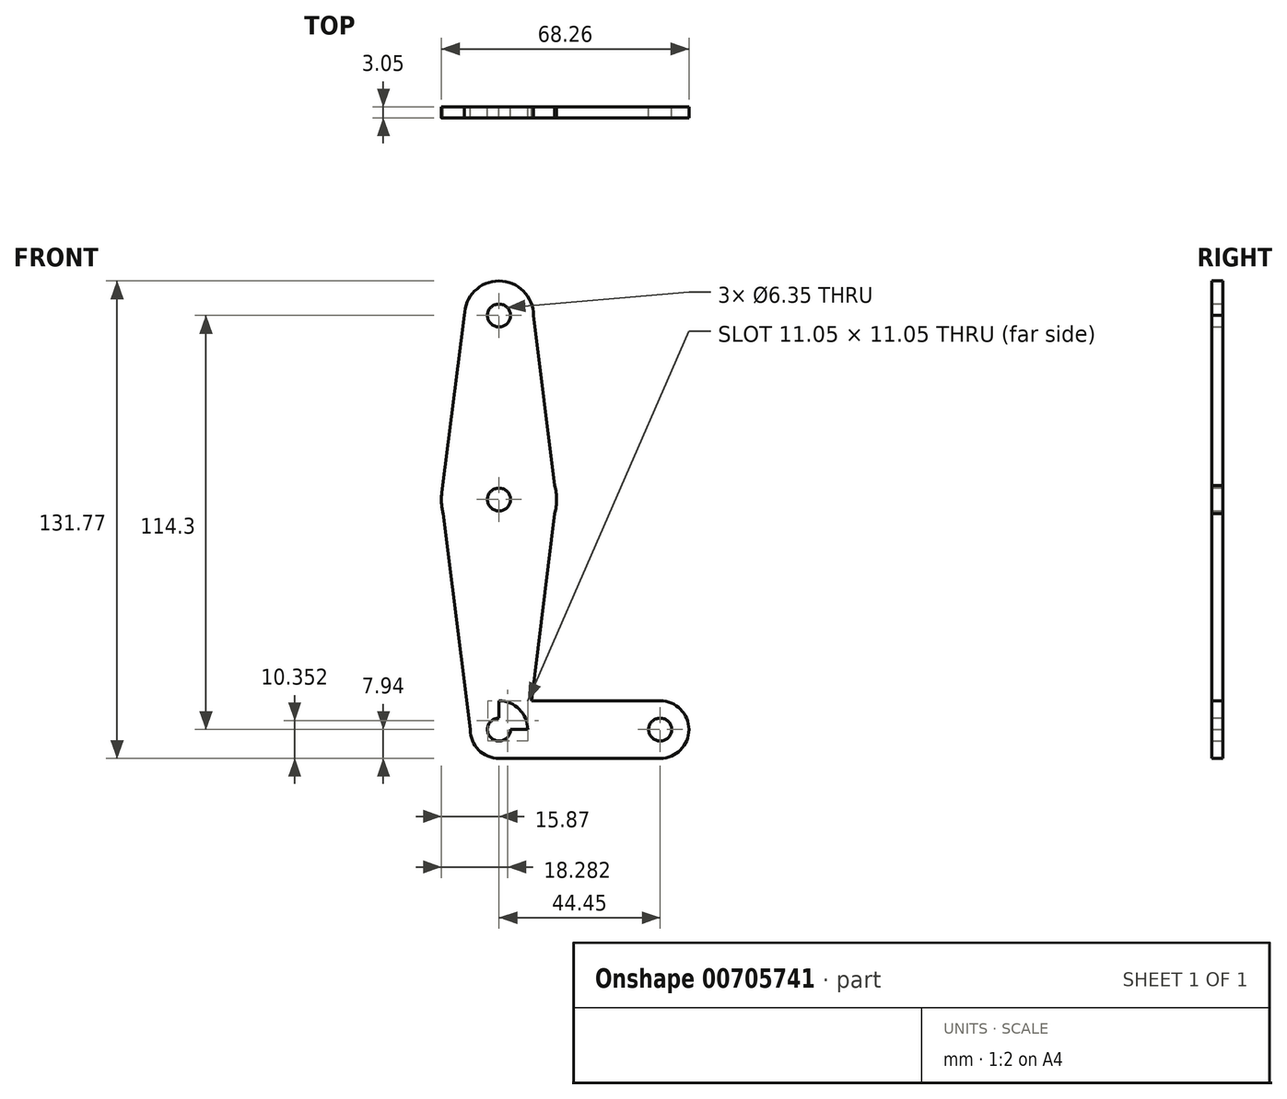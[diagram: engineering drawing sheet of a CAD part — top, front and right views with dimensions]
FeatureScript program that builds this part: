
annotation { "Feature Type Name" : "Feature", "Feature Type Description" : "" }
export const myFeature = defineFeature(function(context is Context, id is Id, definition is map)
    precondition{}
    {
        {
            var Q0;
            Q0=qCreatedBy(makeId("Front.planeOp"),FACE);
            var sketch = newSketch(context, id + "F0", { "sketchPlane" : qUnion([Q0])});
            skLineSegment(sketch, "E0", {"start": v(0, 0) * mm, "end": v(44.45, 0) * mm});
            skLineSegment(sketch, "E1", {"start": v(0, 0) * mm, "end": v(0, 114.3) * mm});
            skCircle(sketch, "E2", {"center": v(44.45, 0) * mm, "radius": 7.94 * mm});
            skCircle(sketch, "E3", {"center": v(0, 0) * mm, "radius": 7.94 * mm});
            skCircle(sketch, "E4", {"center": v(0, 114.3) * mm, "radius": 9.53 * mm});
            skCircle(sketch, "E5", {"center": v(0, 114.3) * mm, "radius": 3.18 * mm});
            skCircle(sketch, "E6", {"center": v(0, 0) * mm, "radius": 3.18 * mm});
            skCircle(sketch, "E7", {"center": v(44.45, 0) * mm, "radius": 3.18 * mm});
            skLineSegment(sketch, "E8", {"start": v(0, 7.94) * mm, "end": v(44.45, 7.94) * mm});
            skLineSegment(sketch, "E9", {"start": v(0, -7.94) * mm, "end": v(44.45, -7.94) * mm});
            skCircle(sketch, "E10", {"center": v(0, 63.5) * mm, "radius": 15.88 * mm});
            skCircle(sketch, "E11", {"center": v(0, 63.5) * mm, "radius": 3.18 * mm});
            skLineSegment(sketch, "E12", {"start": v(-9.53, 114.3) * mm, "end": v(-15.75, 65.5) * mm});
            skLineSegment(sketch, "E13", {"start": v(-15.88, 63.5) * mm, "end": v(-7.94, 0) * mm});
            skLineSegment(sketch, "E14", {"start": v(9.52, 114.3) * mm, "end": v(15.88, 63.5) * mm});
            skLineSegment(sketch, "E15", {"start": v(15.88, 63.5) * mm, "end": v(7.94, 0) * mm});
            skArc(sketch, "E16", {"start": v(9.92, 7.94) * mm, "mid": v(16.58, 11.54) * mm, "end": v(17.2, 19.07) * mm});
            skSolve(sketch);
        }
        {
            var Q0;
            Q0 = qSketchRegion(id + "F0", true);
            extrude(context, id + "F1", {"entities" : qUnion([Q0]), "depth" : 3.05 * mm, "offsetDistance" : 25.4 * mm});
        }
    });
